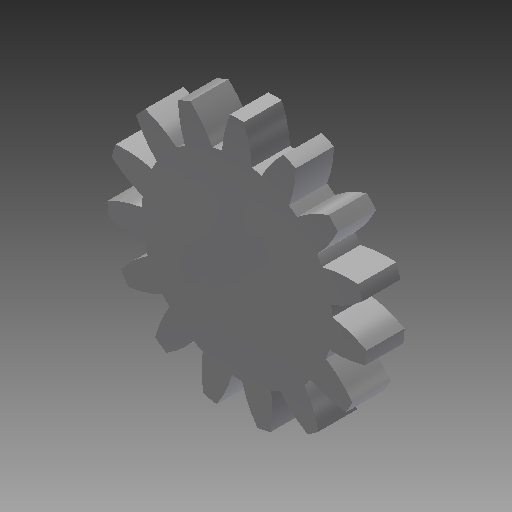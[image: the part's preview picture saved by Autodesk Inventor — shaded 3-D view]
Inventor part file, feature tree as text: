
AUTODESK INVENTOR PART (.ipt)
format: ipt  version: 2017 (Build 210142000, 142)  size: 193,536 bytes
history: native  units: mm (DEFAULTED — no unit token found)
features: plane x3, other x3, sketch x2, extrude x1
ambient origin geometry x8: Origin, YZ Plane, XZ Plane, XY Plane, X Axis, Y Axis, Z Axis, Center Point
bodies: Solid1 (feature_tree)
feature tree (9):
  extrude  "Extrusion1"  Depth=6.35mm TaperAngle=0.0deg
  plane  "Work Plane1"
  plane  "Work Plane2"
  plane  "Work Plane3"
  other  "Spur Gear"
  sketch  "Sketch1"  dims[d0=43.18mm d1=6.35mm d2=0.0mm]
  sketch  "Sketch2"  dims[d3=38.1mm d4=76.2mm d5=0.0mm d6=0.0mm d7=2.094395mm d9=0.0mm d14=0.0mm d15=184.15mm d16=0.0mm d17=0.0mm d18=0.0mm d19=184.15mm]
  other  "Srf1"
  other  "Pitch Diameter"
